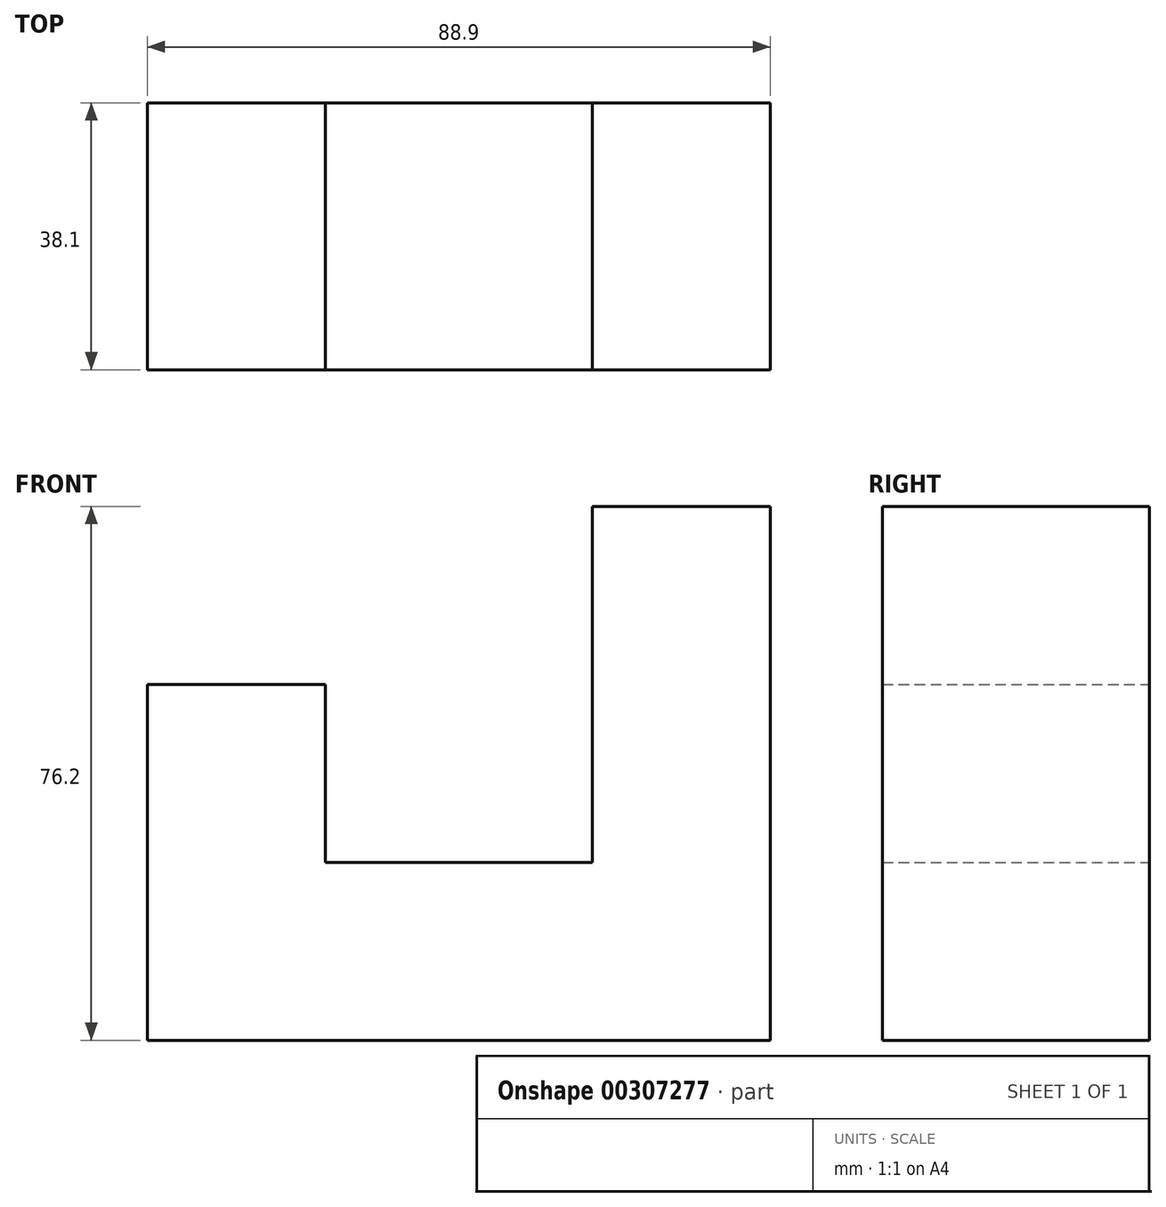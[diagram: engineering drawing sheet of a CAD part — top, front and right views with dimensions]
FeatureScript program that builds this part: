
annotation { "Feature Type Name" : "Feature", "Feature Type Description" : "" }
export const myFeature = defineFeature(function(context is Context, id is Id, definition is map)
    precondition{}
    {
        {
            var Q0;
            Q0=qCreatedBy(makeId("Front.planeOp"),FACE);
            var sketch = newSketch(context, id + "F0", { "sketchPlane" : qUnion([Q0])});
            skLineSegment(sketch, "E0", {"start": v(-44.36, -23.96) * mm, "end": v(44.54, -23.96) * mm});
            skLineSegment(sketch, "E1", {"start": v(44.54, -23.96) * mm, "end": v(44.54, 52.24) * mm});
            skLineSegment(sketch, "E2", {"start": v(44.54, 52.24) * mm, "end": v(19.14, 52.24) * mm});
            skLineSegment(sketch, "E3", {"start": v(19.14, 52.24) * mm, "end": v(19.14, 1.44) * mm});
            skLineSegment(sketch, "E4", {"start": v(19.14, 1.44) * mm, "end": v(-18.96, 1.44) * mm});
            skLineSegment(sketch, "E5", {"start": v(-18.96, 1.44) * mm, "end": v(-18.96, 26.84) * mm});
            skLineSegment(sketch, "E6", {"start": v(-18.96, 26.84) * mm, "end": v(-44.36, 26.84) * mm});
            skLineSegment(sketch, "E7", {"start": v(-44.36, 26.84) * mm, "end": v(-44.36, -23.96) * mm});
            skSolve(sketch);
        }
        {
            var Q0;
            Q0=makeQuery(id+"F0.imprint","IMPRINT",FACE,{"disambiguationData":[TD([[makeQuery(id+"F0.imprint","IMPRINT",EDGE,{"derivedFrom":sQuery(id+"F0.wireOp",EDGE,"E0")}),1.0]])]});
            extrude(context, id + "F1", {"entities" : qUnion([Q0]), "depth" : 38.1 * mm});
        }
    });
